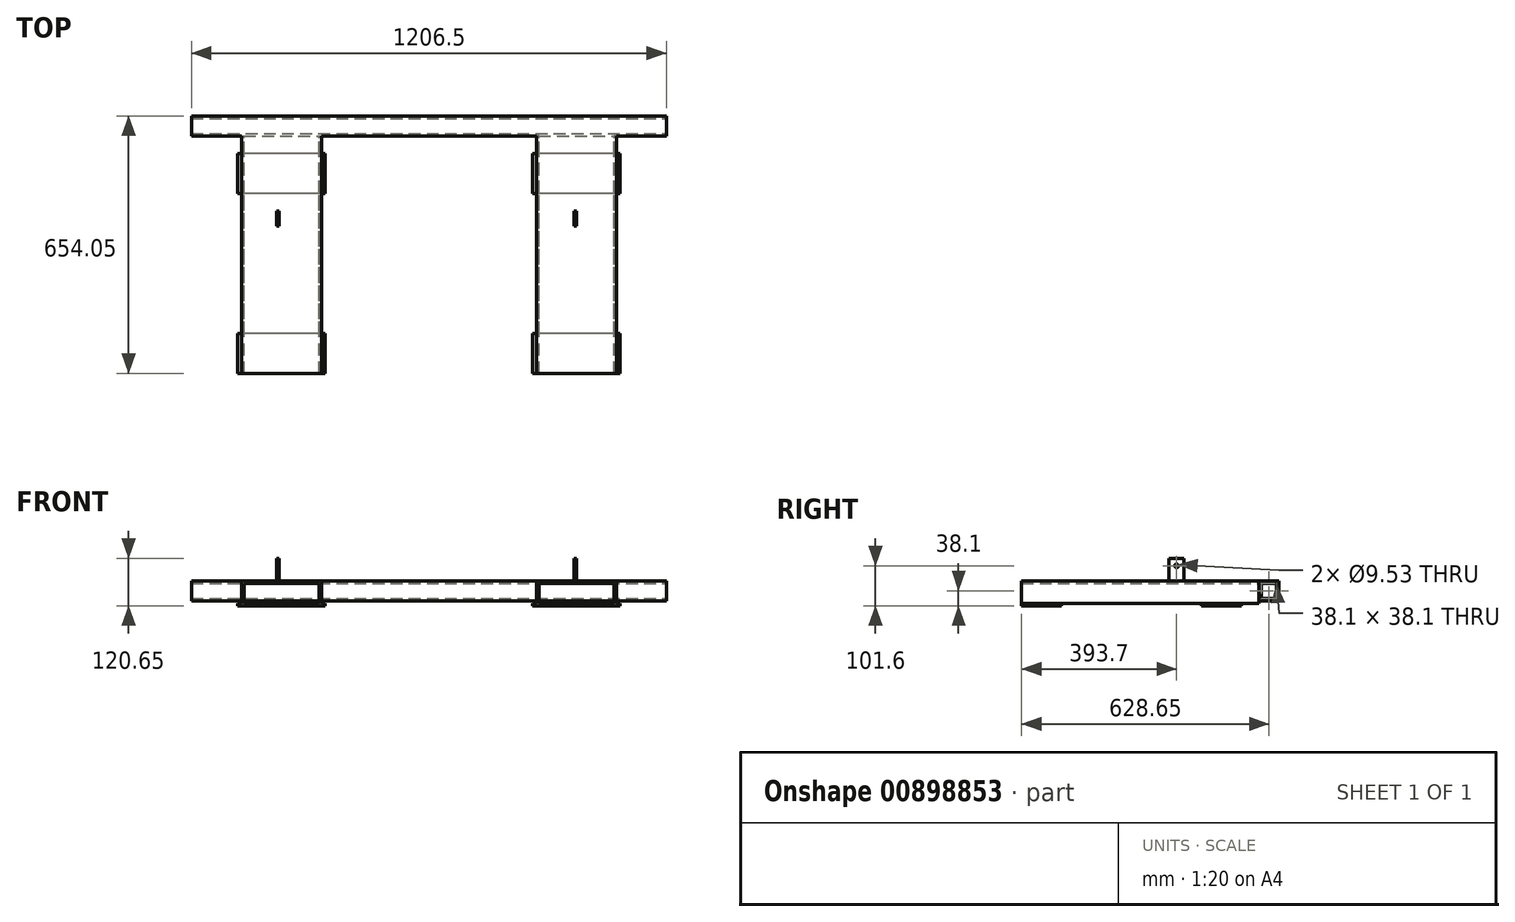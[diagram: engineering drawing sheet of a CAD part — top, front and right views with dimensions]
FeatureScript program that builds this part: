
annotation { "Feature Type Name" : "Feature", "Feature Type Description" : "" }
export const myFeature = defineFeature(function(context is Context, id is Id, definition is map)
    precondition{}
    {
        {
            var Q0;
            Q0=qCreatedBy(makeId("Right.planeOp"),FACE);
            var sketch = newSketch(context, id + "F0", { "sketchPlane" : qUnion([Q0])});
            skLineSegment(sketch, "E0.bottom", {"start": v(-25.4, 25.4) * mm, "end": v(25.4, 25.4) * mm});
            skLineSegment(sketch, "E0.top", {"start": v(-25.4, -25.4) * mm, "end": v(25.4, -25.4) * mm});
            skLineSegment(sketch, "E0.left", {"start": v(-25.4, 25.4) * mm, "end": v(-25.4, -25.4) * mm});
            skLineSegment(sketch, "E0.right", {"start": v(25.4, 25.4) * mm, "end": v(25.4, -25.4) * mm});
            skPoint(sketch, "E0.middle", {"position": v(0, 0) * mm});
            skLineSegment(sketch, "E1.bottom", {"start": v(-19.05, 19.05) * mm, "end": v(19.05, 19.05) * mm});
            skLineSegment(sketch, "E1.top", {"start": v(-19.05, -19.05) * mm, "end": v(19.05, -19.05) * mm});
            skLineSegment(sketch, "E1.left", {"start": v(-19.05, 19.05) * mm, "end": v(-19.05, -19.05) * mm});
            skLineSegment(sketch, "E1.right", {"start": v(19.05, 19.05) * mm, "end": v(19.05, -19.05) * mm});
            skSolve(sketch);
        }
        {
            var Q0;
            Q0=makeQuery(id+"F0.imprint","IMPRINT",FACE,{"disambiguationData":[TD([[makeQuery(id+"F0.imprint","IMPRINT",EDGE,{"derivedFrom":sQuery(id+"F0.wireOp",EDGE,"E0.bottom")}),-1.0]])]});
            extrude(context, id + "F1", {"entities" : qUnion([Q0]), "oppositeDirection" : true, "depth" : 1206.5 * mm, "offsetDistance" : 25.4 * mm});
        }
        {
            var Q0;
            Q0=qCreatedBy(makeId("Front.planeOp"),FACE);
            cPlane(context, id + "F2", {"entities" : qUnion([Q0]), "cplaneType" : CPlaneType.OFFSET, "offset" : 25.4 * mm, "width" : 152.4 * mm, "height" : 152.4 * mm});
        }
        {
            var Q0;
            Q0=qCreatedBy(id+"F2.planeOp",FACE);
            var sketch = newSketch(context, id + "F3", { "sketchPlane" : qUnion([Q0])});
            skLineSegment(sketch, "E2.bottom", {"start": v(-1079.5, 25.4) * mm, "end": v(-876.3, 25.4) * mm});
            skLineSegment(sketch, "E2.top", {"start": v(-1079.5, -31.75) * mm, "end": v(-1073.15, -31.75) * mm});
            skLineSegment(sketch, "E2.left", {"start": v(-1079.5, 25.4) * mm, "end": v(-1079.5, -31.75) * mm});
            skLineSegment(sketch, "E2.right", {"start": v(-876.3, 25.4) * mm, "end": v(-876.3, -31.75) * mm});
            skLineSegment(sketch, "E3.bottom", {"start": v(-127, 25.4) * mm, "end": v(-330.2, 25.4) * mm});
            skLineSegment(sketch, "E3.top", {"start": v(-127, -31.75) * mm, "end": v(-133.35, -31.75) * mm});
            skLineSegment(sketch, "E3.left", {"start": v(-127, 25.4) * mm, "end": v(-127, -31.75) * mm});
            skLineSegment(sketch, "E3.right", {"start": v(-330.2, 25.4) * mm, "end": v(-330.2, -31.75) * mm});
            skLineSegment(sketch, "E4", {"start": v(-1073.15, -31.75) * mm, "end": v(-1073.15, 19.05) * mm});
            skLineSegment(sketch, "E5", {"start": v(-1073.15, 19.05) * mm, "end": v(-882.65, 19.05) * mm});
            skLineSegment(sketch, "E6", {"start": v(-882.65, 19.05) * mm, "end": v(-882.65, -31.75) * mm});
            skLineSegment(sketch, "E7", {"start": v(-323.85, -31.75) * mm, "end": v(-323.85, 19.05) * mm});
            skLineSegment(sketch, "E8", {"start": v(-323.85, 19.05) * mm, "end": v(-133.35, 19.05) * mm});
            skLineSegment(sketch, "E9", {"start": v(-133.35, 19.05) * mm, "end": v(-133.35, -31.75) * mm});
            skLineSegment(sketch, "E10.trimOffspring", {"start": v(-882.65, -31.75) * mm, "end": v(-876.3, -31.75) * mm});
            skLineSegment(sketch, "E11.trimOffspring", {"start": v(-323.85, -31.75) * mm, "end": v(-330.2, -31.75) * mm});
            skSolve(sketch);
        }
        {
            var Q0;
            Q0 = qSketchRegion(id + "F3", true);
            extrude(context, id + "F4", {"entities" : qUnion([Q0]), "operationType" : NewBodyOperationType.ADD, "depth" : 603.25 * mm, "offsetDistance" : 25.4 * mm});
        }
        {
            var Q0;
            Q0=makeQuery(id+"F4.opExtrude","SWEPT_FACE",FACE,{"disambiguationData":[OSD([sQuery(id+"F3.wireOp",EDGE,"E10.trimOffspring")])]});
            var sketch = newSketch(context, id + "F5", { "sketchPlane" : qUnion([Q0])});
            skLineSegment(sketch, "E12.bottom", {"start": v(-117.48, 69.85) * mm, "end": v(-339.73, 69.85) * mm});
            skLineSegment(sketch, "E12.top", {"start": v(-117.48, 171.45) * mm, "end": v(-339.73, 171.45) * mm});
            skLineSegment(sketch, "E12.left", {"start": v(-117.48, 69.85) * mm, "end": v(-117.48, 171.45) * mm});
            skLineSegment(sketch, "E12.right", {"start": v(-339.73, 69.85) * mm, "end": v(-339.73, 171.45) * mm});
            skLineSegment(sketch, "E13.bottom", {"start": v(-117.48, 527.05) * mm, "end": v(-339.73, 527.05) * mm});
            skLineSegment(sketch, "E13.top", {"start": v(-117.48, 628.65) * mm, "end": v(-339.73, 628.65) * mm});
            skLineSegment(sketch, "E13.left", {"start": v(-117.48, 527.05) * mm, "end": v(-117.48, 628.65) * mm});
            skLineSegment(sketch, "E13.right", {"start": v(-339.73, 527.05) * mm, "end": v(-339.73, 628.65) * mm});
            skLineSegment(sketch, "E14.bottom", {"start": v(-866.78, 69.85) * mm, "end": v(-1089.03, 69.85) * mm});
            skLineSegment(sketch, "E14.top", {"start": v(-866.78, 171.45) * mm, "end": v(-1089.03, 171.45) * mm});
            skLineSegment(sketch, "E14.left", {"start": v(-866.78, 69.85) * mm, "end": v(-866.78, 171.45) * mm});
            skLineSegment(sketch, "E14.right", {"start": v(-1089.03, 69.85) * mm, "end": v(-1089.03, 171.45) * mm});
            skLineSegment(sketch, "E15.bottom", {"start": v(-866.78, 527.05) * mm, "end": v(-1089.03, 527.05) * mm});
            skLineSegment(sketch, "E15.top", {"start": v(-866.78, 628.65) * mm, "end": v(-1089.03, 628.65) * mm});
            skLineSegment(sketch, "E15.left", {"start": v(-866.78, 527.05) * mm, "end": v(-866.78, 628.65) * mm});
            skLineSegment(sketch, "E15.right", {"start": v(-1089.03, 527.05) * mm, "end": v(-1089.03, 628.65) * mm});
            skSolve(sketch);
        }
        {
            var Q0;
            Q0 = qSketchRegion(id + "F5", true);
            extrude(context, id + "F6", {"entities" : qUnion([Q0]), "operationType" : NewBodyOperationType.ADD, "depth" : 6.35 * mm, "offsetDistance" : 25.4 * mm});
        }
        {
            var Q0;
            Q0=makeQuery(id+"F4.boolean.opBoolean","MERGE",FACE,{"derivedFrom":[makeQuery(id+"F1.opExtrude","SWEPT_FACE",FACE,{"disambiguationData":[OSD([sQuery(id+"F0.wireOp",EDGE,"E0.bottom")])]}),makeQuery(id+"F4.opExtrude","SWEPT_FACE",FACE,{"disambiguationData":[OSD([sQuery(id+"F3.wireOp",EDGE,"E2.bottom")])]}),makeQuery(id+"F4.opExtrude","SWEPT_FACE",FACE,{"disambiguationData":[OSD([sQuery(id+"F3.wireOp",EDGE,"E3.bottom")])]})]});
            var sketch = newSketch(context, id + "F7", { "sketchPlane" : qUnion([Q0])});
            skLineSegment(sketch, "E16.bottom", {"start": v(-234.95, -215.9) * mm, "end": v(-228.6, -215.9) * mm});
            skLineSegment(sketch, "E16.top", {"start": v(-234.95, -254) * mm, "end": v(-228.6, -254) * mm});
            skLineSegment(sketch, "E16.left", {"start": v(-234.95, -215.9) * mm, "end": v(-234.95, -254) * mm});
            skLineSegment(sketch, "E16.right", {"start": v(-228.6, -215.9) * mm, "end": v(-228.6, -254) * mm});
            skLineSegment(sketch, "E17.bottom", {"start": v(-990.6, -215.9) * mm, "end": v(-984.25, -215.9) * mm});
            skLineSegment(sketch, "E17.top", {"start": v(-990.6, -254) * mm, "end": v(-984.25, -254) * mm});
            skLineSegment(sketch, "E17.left", {"start": v(-990.6, -215.9) * mm, "end": v(-990.6, -254) * mm});
            skLineSegment(sketch, "E17.right", {"start": v(-984.25, -215.9) * mm, "end": v(-984.25, -254) * mm});
            skSolve(sketch);
        }
        {
            var Q0;
            Q0 = qSketchRegion(id + "F7", true);
            extrude(context, id + "F8", {"entities" : qUnion([Q0]), "operationType" : NewBodyOperationType.ADD, "depth" : 57.15 * mm, "offsetDistance" : 25.4 * mm});
        }
        {
            var Q0;
            Q0=makeQuery(id+"F8.opExtrude","SWEPT_FACE",FACE,{"disambiguationData":[OSD([sQuery(id+"F7.wireOp",EDGE,"E16.right")])]});
            var sketch = newSketch(context, id + "F9", { "sketchPlane" : qUnion([Q0])});
            skCircle(sketch, "E18", {"center": v(-234.95, 63.5) * mm, "radius": 4.76 * mm});
            skSolve(sketch);
        }
        {
            var Q0;
            Q0 = qSketchRegion(id + "F9", true);
            extrude(context, id + "F10", {"entities" : qUnion([Q0]), "operationType" : NewBodyOperationType.REMOVE, "oppositeDirection" : true, "depth" : 762 * mm, "offsetDistance" : 25.4 * mm});
        }
    });
